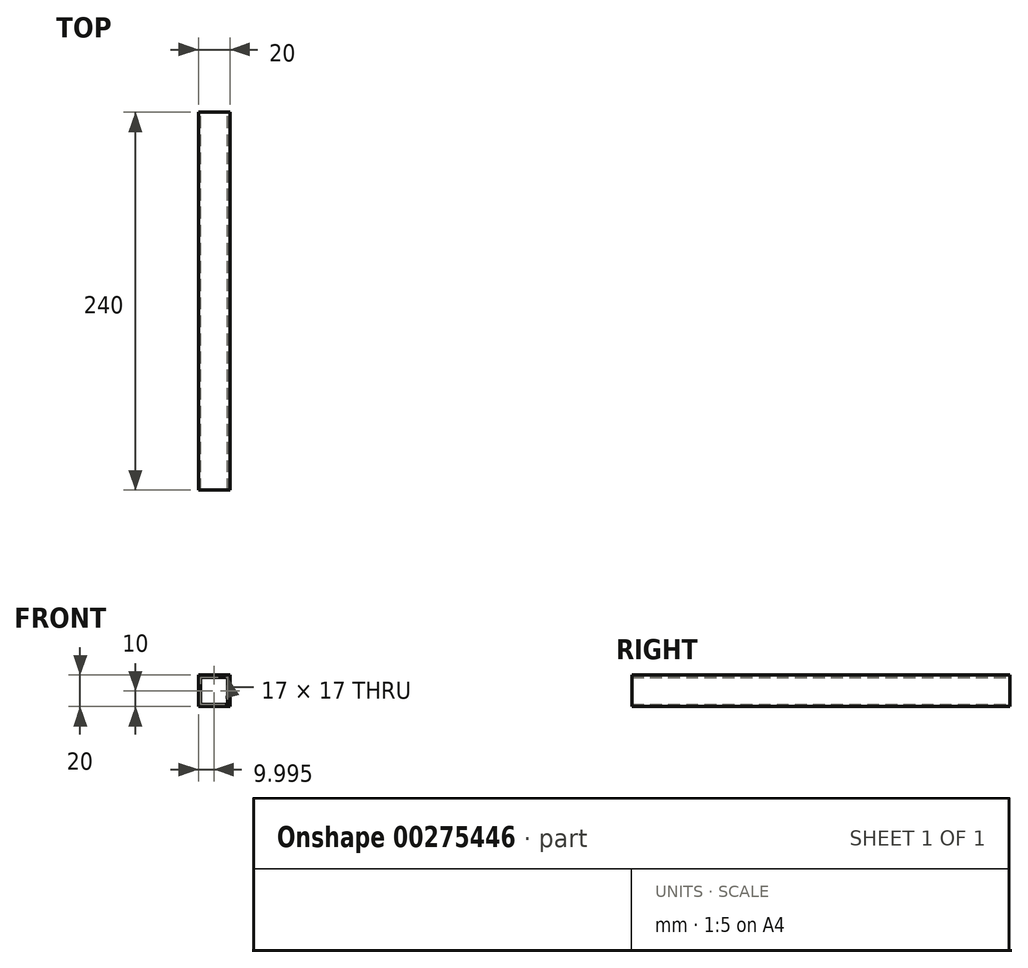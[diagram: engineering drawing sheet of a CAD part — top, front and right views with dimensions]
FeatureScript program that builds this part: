
annotation { "Feature Type Name" : "Feature", "Feature Type Description" : "" }
export const myFeature = defineFeature(function(context is Context, id is Id, definition is map)
    precondition{}
    {
        {
            var Q0;
            Q0=qCreatedBy(makeId("Front.planeOp"),FACE);
            var sketch = newSketch(context, id + "F0", { "sketchPlane" : qUnion([Q0])});
            skLineSegment(sketch, "E0.bottom", {"start": v(-34.48, 27.75) * mm, "end": v(-54.48, 27.75) * mm});
            skLineSegment(sketch, "E0.top", {"start": v(-34.48, 47.75) * mm, "end": v(-54.48, 47.75) * mm});
            skLineSegment(sketch, "E0.left", {"start": v(-34.48, 27.75) * mm, "end": v(-34.48, 47.75) * mm});
            skLineSegment(sketch, "E0.right", {"start": v(-54.48, 27.75) * mm, "end": v(-54.48, 47.75) * mm});
            skPoint(sketch, "E0.middle", {"position": v(-44.48, 37.75) * mm});
            skLineSegment(sketch, "E1.bottom", {"start": v(-35.98, 29.25) * mm, "end": v(-52.98, 29.25) * mm});
            skLineSegment(sketch, "E1.top", {"start": v(-35.98, 46.25) * mm, "end": v(-52.98, 46.25) * mm});
            skLineSegment(sketch, "E1.left", {"start": v(-35.98, 29.25) * mm, "end": v(-35.98, 46.25) * mm});
            skLineSegment(sketch, "E1.right", {"start": v(-52.98, 29.25) * mm, "end": v(-52.98, 46.25) * mm});
            skSolve(sketch);
        }
        {
            var Q0;
            Q0=makeQuery(id+"F0.imprint","IMPRINT",FACE,{"disambiguationData":[TD([[makeQuery(id+"F0.imprint","IMPRINT",EDGE,{"derivedFrom":sQuery(id+"F0.wireOp",EDGE,"E0.bottom")}),-1.0]])]});
            extrude(context, id + "F1", {"entities" : qUnion([Q0]), "depth" : 240 * mm});
        }
    });
